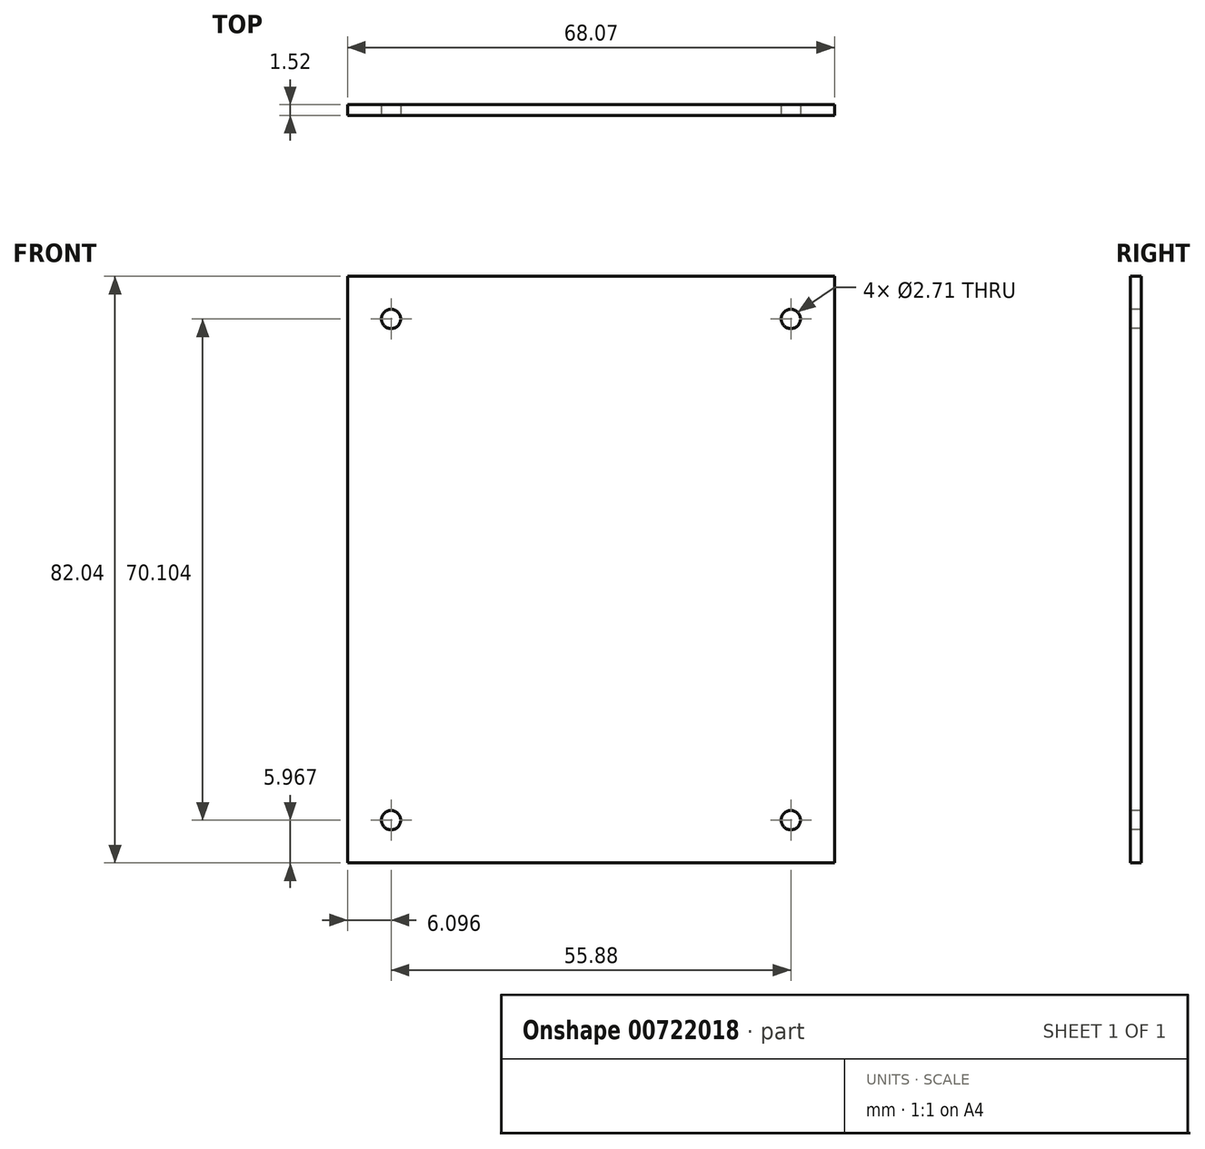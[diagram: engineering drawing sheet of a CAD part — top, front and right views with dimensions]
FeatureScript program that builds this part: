
annotation { "Feature Type Name" : "Feature", "Feature Type Description" : "" }
export const myFeature = defineFeature(function(context is Context, id is Id, definition is map)
    precondition{}
    {
        {
            var Q0;
            Q0=qCreatedBy(makeId("Front.planeOp"),FACE);
            var sketch = newSketch(context, id + "F0", { "sketchPlane" : qUnion([Q0])});
            skLineSegment(sketch, "E0.bottom", {"start": v(0, 0) * mm, "end": v(68.07, 0) * mm});
            skLineSegment(sketch, "E0.top", {"start": v(0, -82.04) * mm, "end": v(68.07, -82.04) * mm});
            skLineSegment(sketch, "E0.left", {"start": v(0, 0) * mm, "end": v(0, -82.04) * mm});
            skLineSegment(sketch, "E0.right", {"start": v(68.07, 0) * mm, "end": v(68.07, -82.04) * mm});
            skSolve(sketch);
        }
        {
            var Q0;
            Q0 = qSketchRegion(id + "F0", true);
            extrude(context, id + "F1", {"entities" : qUnion([Q0]), "depth" : 1.52 * mm, "offsetDistance" : 25.4 * mm});
        }
        {
            var Q0;
            Q0=makeQuery(id+"F1.opExtrude","CAP_FACE",FACE,{"disambiguationData":[OSD([sQuery(id+"F0.wireOp",EDGE,"E0.bottom"),sQuery(id+"F0.wireOp",EDGE,"E0.top"),sQuery(id+"F0.wireOp",EDGE,"E0.left"),sQuery(id+"F0.wireOp",EDGE,"E0.right")])],"isStart":false});
            var sketch = newSketch(context, id + "F2", { "sketchPlane" : qUnion([Q0])});
            skPoint(sketch, "E1", {"position": v(6.1, -5.97) * mm});
            skPoint(sketch, "E2", {"position": v(61.98, -5.97) * mm});
            skPoint(sketch, "E3", {"position": v(61.98, -76.07) * mm});
            skPoint(sketch, "E4", {"position": v(6.1, -76.07) * mm});
            skLineSegment(sketch, "E5", {"start": v(34.04, 0) * mm, "end": v(34.04, -82.04) * mm, "construction": true});
            skLineSegment(sketch, "E6", {"start": v(68.07, -41.02) * mm, "end": v(0, -41.02) * mm, "construction": true});
            skSolve(sketch);
        }
        {
            var Q0;
            Q0=sQuery(id+"F2.wireOp",VERTEX,"E1");
            var Q1;
            Q1=sQuery(id+"F2.wireOp",VERTEX,"E2");
            var Q2;
            Q2=sQuery(id+"F2.wireOp",VERTEX,"E3");
            var Q3;
            Q3=sQuery(id+"F2.wireOp",VERTEX,"E4");
            var Q4;
            Q4=makeQuery(id+"F1.opExtrude","SWEPT_BODY",BODY,{"disambiguationData":[OSD([sQuery(id+"F0.wireOp",EDGE,"E0.bottom"),sQuery(id+"F0.wireOp",EDGE,"E0.top"),sQuery(id+"F0.wireOp",EDGE,"E0.left"),sQuery(id+"F0.wireOp",EDGE,"E0.right")])]});
            hole(context, id + "F3", {"style" : HoleStyle.SIMPLE, "endStyle" : HoleEndStyle.THROUGH, "standardTappedOrClearance" : lookupTablePath({ "standard" : "ANSI", "engagement" : "75%", "pitch" : "32 tpi", "size" : "#6", "type" : "Tapped" }), "standardBlindInLast" : lookupTablePath({ "standard" : "ANSI", "engagement" : "75%", "pitch" : "32 tpi", "size" : "#6", "type" : "Tapped" }), "holeDiameter" : 2.7 * mm, "majorDiameter" : 3.5 * mm, "showTappedDepth" : true, "isTappedThrough" : true, "tappedDepth" : 10.32 * mm, "tapClearance" : 3, "startFromSketch" : true, "locations" : qUnion([Q0, Q1, Q2, Q3]), "scope" : qUnion([Q4])});
        }
    });
